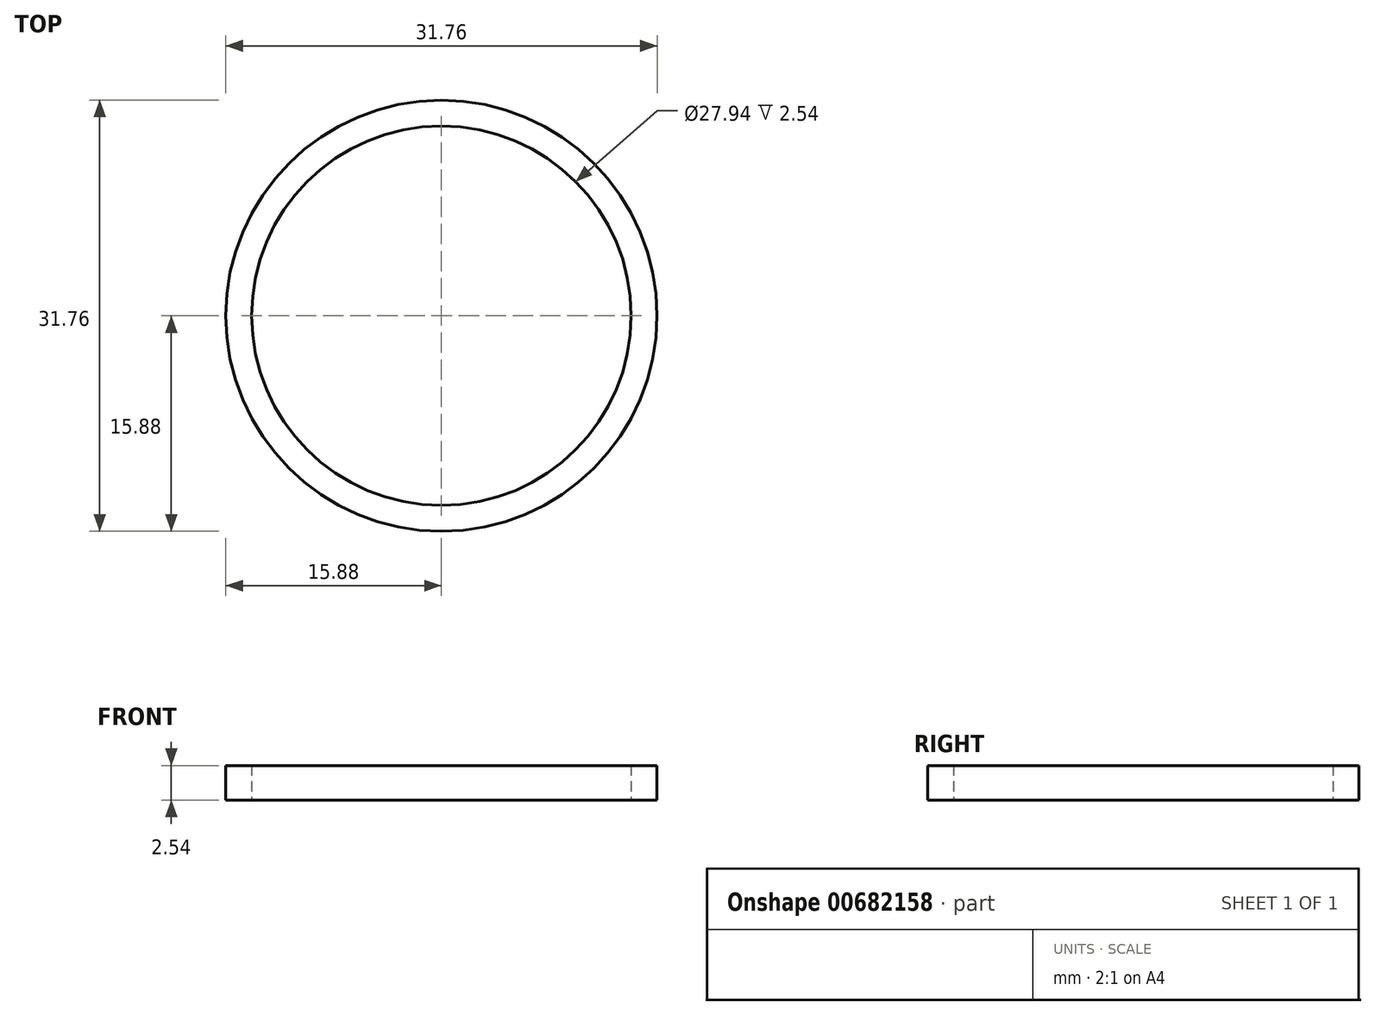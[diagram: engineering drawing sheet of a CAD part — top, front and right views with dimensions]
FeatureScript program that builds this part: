
annotation { "Feature Type Name" : "Feature", "Feature Type Description" : "" }
export const myFeature = defineFeature(function(context is Context, id is Id, definition is map)
    precondition{}
    {
        {
            var Q0;
            Q0=qCreatedBy(makeId("Top.planeOp"),FACE);
            var sketch = newSketch(context, id + "F0", { "sketchPlane" : qUnion([Q0])});
            skCircle(sketch, "E0", {"center": v(0, 0) * mm, "radius": 15.88 * mm});
            skCircle(sketch, "E1", {"center": v(0, 0) * mm, "radius": 13.97 * mm});
            skSolve(sketch);
        }
        {
            var Q0;
            Q0 = qSketchRegion(id + "F0", true);
            extrude(context, id + "F1", {"entities" : qUnion([Q0]), "depth" : 2.54 * mm, "offsetDistance" : 25.4 * mm});
        }
    });
